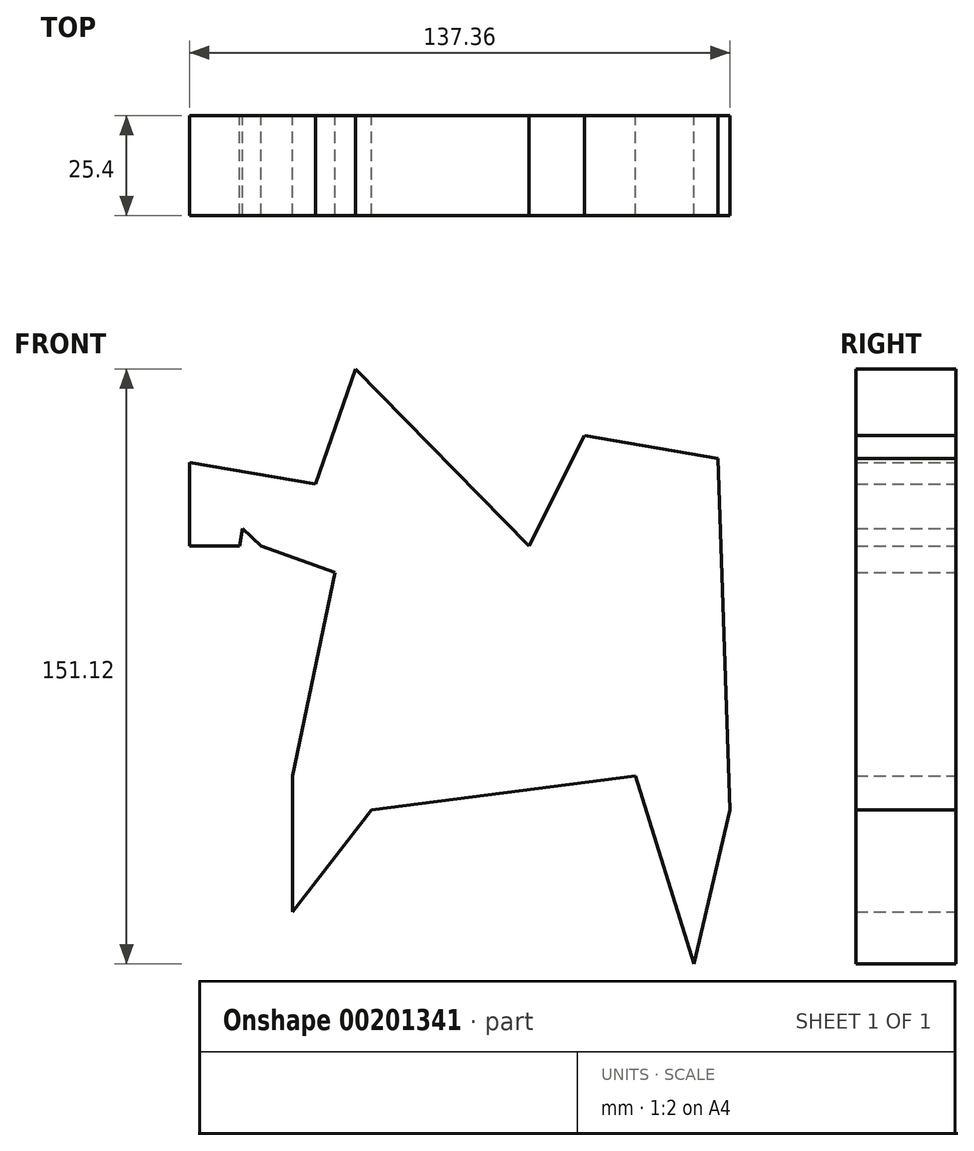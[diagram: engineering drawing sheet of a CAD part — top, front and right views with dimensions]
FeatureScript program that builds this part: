
annotation { "Feature Type Name" : "Feature", "Feature Type Description" : "" }
export const myFeature = defineFeature(function(context is Context, id is Id, definition is map)
    precondition{}
    {
        {
            var Q0;
            Q0=qCreatedBy(makeId("Front.planeOp"),FACE);
            var sketch = newSketch(context, id + "F0", { "sketchPlane" : qUnion([Q0])});
            skLineSegment(sketch, "E0", {"start": v(-27.09, 29.4) * mm, "end": v(-37.86, -22.31) * mm});
            skLineSegment(sketch, "E1", {"start": v(-37.86, -22.31) * mm, "end": v(-37.86, -56.79) * mm});
            skLineSegment(sketch, "E2", {"start": v(-37.86, -56.79) * mm, "end": v(-17.85, -30.93) * mm});
            skLineSegment(sketch, "E3", {"start": v(-17.85, -30.93) * mm, "end": v(49.25, -22.31) * mm});
            skLineSegment(sketch, "E4", {"start": v(49.25, -22.31) * mm, "end": v(64.02, -70.02) * mm});
            skLineSegment(sketch, "E5", {"start": v(64.02, -70.02) * mm, "end": v(73.25, -30.93) * mm});
            skLineSegment(sketch, "E6", {"start": v(73.25, -30.93) * mm, "end": v(70.18, 58.33) * mm});
            skLineSegment(sketch, "E7", {"start": v(70.18, 58.33) * mm, "end": v(36.32, 64.17) * mm});
            skLineSegment(sketch, "E8", {"start": v(36.32, 64.17) * mm, "end": v(22.16, 36.17) * mm});
            skLineSegment(sketch, "E9", {"start": v(22.16, 36.17) * mm, "end": v(-21.85, 81.1) * mm});
            skLineSegment(sketch, "E10", {"start": v(-21.85, 81.1) * mm, "end": v(-32, 51.86) * mm});
            skLineSegment(sketch, "E11", {"start": v(-32, 51.86) * mm, "end": v(-64.11, 57.4) * mm});
            skLineSegment(sketch, "E12", {"start": v(-64.11, 57.4) * mm, "end": v(-64.11, 36.17) * mm});
            skLineSegment(sketch, "E13", {"start": v(-64.11, 36.17) * mm, "end": v(-51.4, 36.17) * mm});
            skLineSegment(sketch, "E14", {"start": v(-51.4, 36.17) * mm, "end": v(-50.62, 40.66) * mm});
            skLineSegment(sketch, "E15", {"start": v(-50.62, 40.66) * mm, "end": v(-45.86, 36.17) * mm});
            skLineSegment(sketch, "E16", {"start": v(-45.86, 36.17) * mm, "end": v(-27.09, 29.4) * mm});
            skSolve(sketch);
        }
        {
            var Q0;
            Q0=makeQuery(id+"F0.imprint","IMPRINT",FACE,{"disambiguationData":[TD([[makeQuery(id+"F0.imprint","IMPRINT",EDGE,{"derivedFrom":sQuery(id+"F0.wireOp",EDGE,"E0")}),1.0]])]});
            extrude(context, id + "F1", {"entities" : qUnion([Q0]), "depth" : 25.4 * mm});
        }
    });
